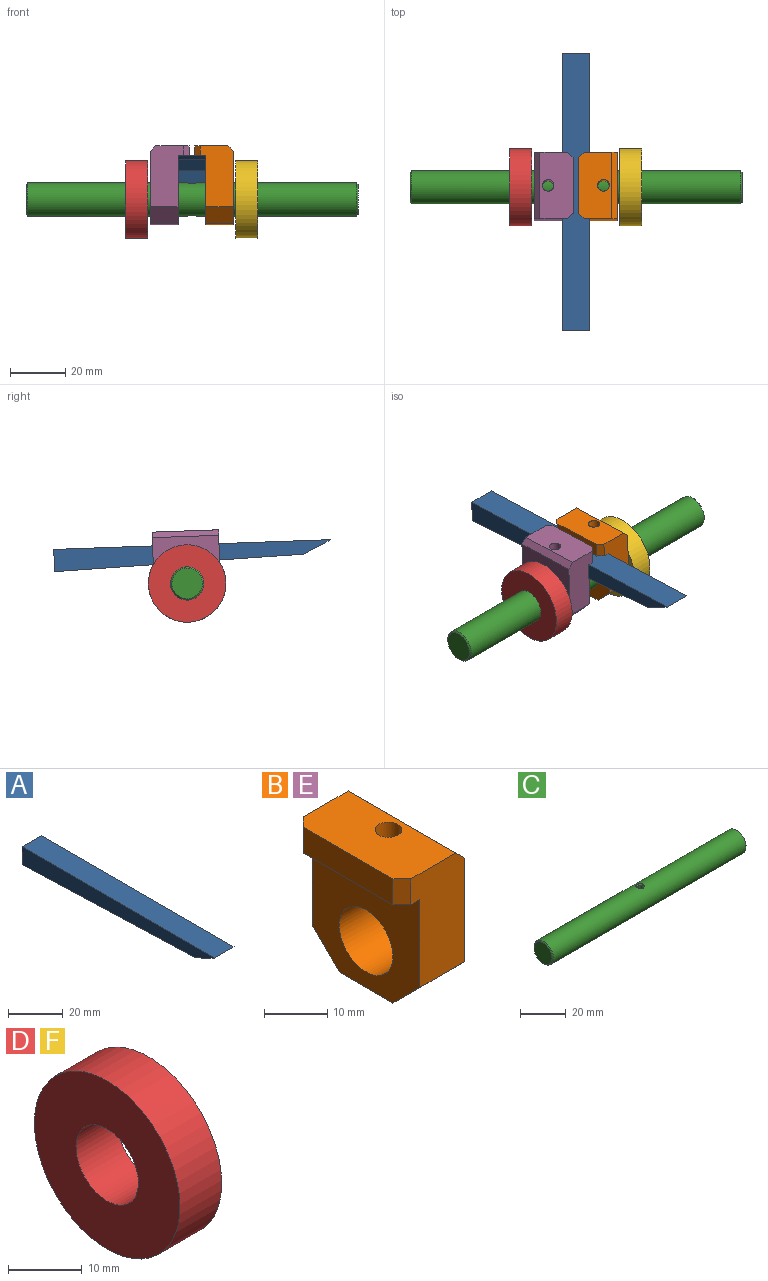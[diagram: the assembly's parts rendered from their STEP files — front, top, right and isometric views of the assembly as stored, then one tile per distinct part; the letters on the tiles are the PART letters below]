
ASSEMBLY  parts=6 mates=8
PART A: 7 faces, bbox 10x100x8 mm
  f0: plane 90x10mm, normal (0,-0.03,-1), area 900.5mm2, adj f1,f4,f5,f6
  f1: plane 10x8.03mm, normal (0,1,0), area 80.3mm2, adj f0,f2,f5,f6
  f2: plane 100x10mm, normal (0,0,1), area 1000mm2, adj f1,f3,f5,f6
  f3: plane 10x2mm, normal (0,-0.5,-0.87), area 23.1mm2, adj f2,f4,f5,f6
  f4: plane 10x8mm, normal (0,-0.42,-0.91), area 88.3mm2, adj f0,f3,f5,f6
  f5: plane 100x8.03mm, normal (-1,0,0), area 606.4mm2, adj f0,f1,f2,f3,f4
  f6: plane 100x8.03mm, normal (1,0,0), area 606.4mm2, adj f0,f1,f2,f3,f4
PART B: 15 faces, bbox 14x24x28 mm
  f0: cylinder r=6mm len=12mm, axis (-1,0,0), area 362.9mm2, adj f4,f6,f9
  f1: plane 24x12mm, normal (0,0,1), area 270.1mm2, adj f2,f7,f8,f9,f12,f13,f14
  f2: plane 20x5mm, normal (-1,0,0), area 100mm2, adj f1,f3,f12,f14
  f3: plane 24x4mm, normal (0,0,-1), area 92mm2, adj f2,f4,f7,f8,f12,f14
  f4: plane 24x23mm, normal (-1,0,0), area 402.9mm2, adj f0,f3,f5,f7,f8,f10,f11
  f5: plane 12x10mm, normal (0,0,-1), area 120mm2, adj f4,f6,f10,f11
  f6: plane 26x24mm, normal (1,0,0), area 474.9mm2, adj f0,f5,f7,f8,f10,f11,f13
  f7: plane 22x12mm, normal (0,-1,0), area 228mm2, adj f1,f3,f4,f6,f11,f13,f14
  f8: plane 22x12mm, normal (0,1,0), area 228mm2, adj f1,f3,f4,f6,f10,f12,f13
  f9: cylinder r=2.1mm len=13.38mm, axis (0,0,1), area 174mm2, adj f0,f1
  f10: plane 10x6mm, normal (0,0.71,-0.71), area 84.9mm2, adj f4,f5,f6,f8
  f11: plane 10x6mm, normal (0,-0.71,-0.71), area 84.9mm2, adj f4,f5,f6,f7
  f12: plane 5x2mm, normal (-0.71,0.71,0), area 14.1mm2, adj f1,f2,f3,f8
  f13: plane 24x2mm, normal (0.71,0,0.71), area 67.9mm2, adj f1,f6,f7,f8
  f14: plane 5x2mm, normal (-0.71,-0.71,0), area 14.1mm2, adj f1,f2,f3,f7
PART C: 8 faces, bbox 120x12x12 mm
  f0: cylinder r=6mm len=119mm, axis (-1,0,0), area 4464.9mm2, adj f4,f5,f6,f7
  f1: plane 11x11mm, normal (1,0,0), area 95mm2, adj f4
  f2: plane 11x11mm, normal (-1,0,0), area 95mm2, adj f5
  f3: cylinder r=1.25mm len=11mm, axis (0,0,-1), area 86.4mm2, adj f6,f7
  f4: cone r=5.5mm half-angle=45deg, axis (-1,0,0), area 25.5mm2, adj f0,f1
  f5: cone r=6mm half-angle=45deg, axis (1,0,0), area 25.5mm2, adj f0,f2
  f6: bspline ~3.82x3.5mm, area 7.4mm2, adj f0,f3
  f7: bspline ~3.82x3.5mm, area 7.4mm2, adj f0,f3
PART D: 4 faces, bbox 8x28x28 mm
  f0: cylinder r=6mm len=12mm, axis (-1,0,0), area 301.6mm2, adj f2,f3
  f1: cylinder r=14mm len=28mm, axis (-1,0,0), area 703.7mm2, adj f2,f3
  f2: plane 28x28mm, normal (1,0,0), area 502.7mm2, adj f0,f1
  f3: plane 28x28mm, normal (-1,0,0), area 502.7mm2, adj f0,f1
PART E: same geometry as B
PART F: same geometry as D
PLACE A rot(axis=(-1,0,0),2deg) t=(-0.14,1.78,7.08)mm
PLACE B rot(axis=(-1,0,0),2deg) t=(-0.14,1.78,7.08)mm
PLACE C t=(-5.09,1.78,7.08)mm fixed
PLACE D rot(axis=(1,0,0),20.5deg) t=(-29.07,1.78,7.08)mm
PLACE E rot(axis=(0,-0.02,-1),180deg) t=(-10.14,1.78,7.08)mm
PLACE F rot(axis=(0,1,0),180deg) t=(18.73,1.78,7.08)mm
MATE planar A.f6 <-> B.f4  axis (1,0,0) through (-0.14,-47.98,21.69)mm
MATE planar E.f4 <-> A.f5  axis (1,0,0) through (-10.14,1.92,11.13)mm
MATE cylindrical D.f0 <-> C.f0  axis (-1,0,0) through (-25.07,1.78,7.08)mm
MATE planar A.f2 <-> B.f3  axis (0,0.04,1) through (-5.14,0.03,21.15)mm
MATE slider F.f0 <-> C.f0  axis (1,0,0) through (14.73,1.78,7.08)mm
MATE parallel E.f3 <-> A.f2  axis (0,-0.04,-1) through (-8.2,2.27,21.07)mm
MATE cylindrical B.f0 <-> C.f0  axis (-1,0,0) through (4.86,1.78,7.08)mm
MATE cylindrical E.f0 <-> C.f0  axis (1,0,0) through (-15.14,1.78,7.08)mm
